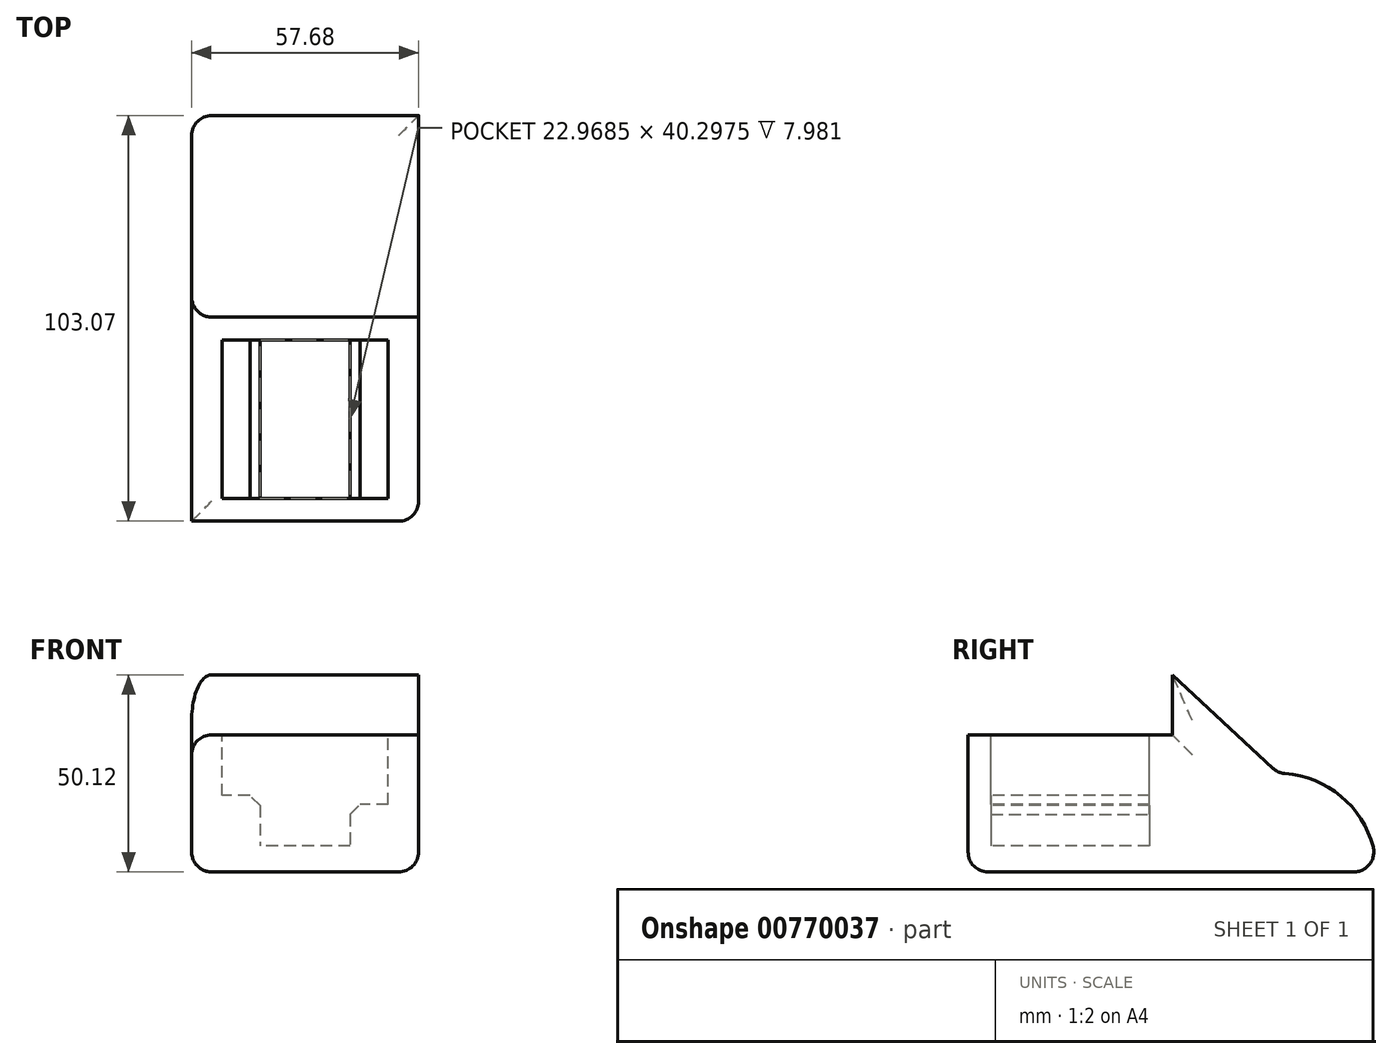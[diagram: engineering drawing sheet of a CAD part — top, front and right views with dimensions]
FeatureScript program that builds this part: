
annotation { "Feature Type Name" : "Feature", "Feature Type Description" : "" }
export const myFeature = defineFeature(function(context is Context, id is Id, definition is map)
    precondition{}
    {
        {
            var Q0;
            Q0=qCreatedBy(makeId("Top.planeOp"),FACE);
            var sketch = newSketch(context, id + "F0", { "sketchPlane" : qUnion([Q0])});
            skLineSegment(sketch, "E0.bottom", {"start": v(28.84, 51.86) * mm, "end": v(-28.84, 51.86) * mm});
            skLineSegment(sketch, "E0.top", {"start": v(28.84, -51.86) * mm, "end": v(-28.84, -51.86) * mm});
            skLineSegment(sketch, "E0.left", {"start": v(28.84, 51.86) * mm, "end": v(28.84, -51.86) * mm});
            skLineSegment(sketch, "E0.right", {"start": v(-28.84, 51.86) * mm, "end": v(-28.84, -51.86) * mm});
            skPoint(sketch, "E0.middle", {"position": v(0, 0) * mm});
            skSolve(sketch);
        }
        {
            var Q0;
            Q0 = qSketchRegion(id + "F0", true);
            extrude(context, id + "F1", {"entities" : qUnion([Q0]), "depth" : 50.12 * mm, "offsetDistance" : 25.4 * mm});
        }
        {
            var Q0;
            Q0=makeQuery(id+"F1.opExtrude","SWEPT_FACE",FACE,{"disambiguationData":[OSD([sQuery(id+"F0.wireOp",EDGE,"E0.left")])]});
            var sketch = newSketch(context, id + "F2", { "sketchPlane" : qUnion([Q0])});
            skArc(sketch, "E1", {"start": v(51.86, 0) * mm, "mid": v(44.58, 17.66) * mm, "end": v(26.97, 25.06) * mm});
            skPoint(sketch, "E1.endSnap0", {"position": v(51.86, 25.06) * mm});
            skLineSegment(sketch, "E2", {"start": v(26.97, 25.06) * mm, "end": v(0, 50.12) * mm});
            skLineSegment(sketch, "E3", {"start": v(0, 50.12) * mm, "end": v(0, 34.85) * mm});
            skLineSegment(sketch, "E4", {"start": v(0, 34.85) * mm, "end": v(-51.86, 34.85) * mm});
            skSolve(sketch);
        }
        {
            var Q0;
            Q0=makeQuery(id+"F2.imprint","IMPRINT",FACE,{"disambiguationData":[TD([[makeQuery(id+"F2.imprint","IMPRINT",EDGE,{"derivedFrom":sQuery(id+"F2.wireOp",EDGE,"E1")}),-1.0]])]});
            var Q1;
            {var subQ0=sQuery(id+"F2.wireOp",EDGE,"E3");Q1=makeQuery(id+"F2.imprint","IMPRINT",FACE,{"disambiguationData":[TD([[makeQuery(id+"F2.imprint","IMPRINT",EDGE,{"derivedFrom":subQ0}),-1.0]])]});}
            extrude(context, id + "F3", {"entities" : qUnion([Q0, Q1]), "operationType" : NewBodyOperationType.REMOVE, "oppositeDirection" : true, "depth" : 280.97 * mm, "offsetDistance" : 25.4 * mm});
        }
        {
            var Q0;
            Q0=makeQuery(id+"F3.boolean.opBoolean","COPY",FACE,{"derivedFrom":makeQuery(id+"F3.opExtrude","SWEPT_FACE",FACE,{"disambiguationData":[OSD([sQuery(id+"F2.wireOp",EDGE,"E4")])]})});
            var sketch = newSketch(context, id + "F4", { "sketchPlane" : qUnion([Q0])});
            skLineSegment(sketch, "E5.bottom", {"start": v(21.13, -5.78) * mm, "end": v(-21.13, -5.78) * mm});
            skLineSegment(sketch, "E5.top", {"start": v(21.13, -46.08) * mm, "end": v(-21.13, -46.08) * mm});
            skLineSegment(sketch, "E5.left", {"start": v(21.13, -5.78) * mm, "end": v(21.13, -46.08) * mm});
            skLineSegment(sketch, "E5.right", {"start": v(-21.13, -5.78) * mm, "end": v(-21.13, -46.08) * mm});
            skPoint(sketch, "E5.middle", {"position": v(0, -25.93) * mm});
            skPoint(sketch, "E5.middle.positionSnap0", {"position": v(-28.84, -25.93) * mm});
            skPoint(sketch, "E5.centerSnap0", {"position": v(-28.84, -25.93) * mm});
            skSolve(sketch);
        }
        {
            var Q0;
            Q0=makeQuery(id+"F4.imprint","IMPRINT",FACE,{"disambiguationData":[TD([[makeQuery(id+"F4.imprint","IMPRINT",EDGE,{"derivedFrom":sQuery(id+"F4.wireOp",EDGE,"E5.bottom")}),1.0]])]});
            extrude(context, id + "F5", {"entities" : qUnion([Q0]), "operationType" : NewBodyOperationType.REMOVE, "oppositeDirection" : true, "depth" : 28.22 * mm, "offsetDistance" : 25.4 * mm});
        }
        {
            var Q0;
            Q0=makeQuery(id+"F5.boolean.opBoolean","COPY",FACE,{"derivedFrom":makeQuery(id+"F5.opExtrude","CAP_FACE",FACE,{"disambiguationData":[OSD([sQuery(id+"F4.wireOp",EDGE,"E5.bottom"),sQuery(id+"F4.wireOp",EDGE,"E5.top"),sQuery(id+"F4.wireOp",EDGE,"E5.left"),sQuery(id+"F4.wireOp",EDGE,"E5.right")])],"isStart":false})});
            var sketch = newSketch(context, id + "F6", { "sketchPlane" : qUnion([Q0])});
            skLineSegment(sketch, "E6", {"start": v(-11.5, -5.78) * mm, "end": v(-11.5, -46.08) * mm});
            skSolve(sketch);
        }
        {
            var Q0;
            {var subQ0=sQuery(id+"F6.wireOp",EDGE,"E6");Q0=makeQuery(id+"F6.imprint","IMPRINT",FACE,{"disambiguationData":[TD([[makeQuery(id+"F6.imprint","IMPRINT",EDGE,{"derivedFrom":subQ0}),-1.0]])]});}
            var Q1;
            Q1 = qSketchRegion(id + "F6", true);
            extrude(context, id + "F7", {"entities" : qUnion([Q0, Q1]), "operationType" : NewBodyOperationType.ADD, "depth" : 12.77 * mm, "offsetDistance" : 25.4 * mm});
        }
        {
            var Q0;
            Q0=makeQuery(id+"F5.boolean.opBoolean","COPY",FACE,{"derivedFrom":makeQuery(id+"F5.opExtrude","CAP_FACE",FACE,{"disambiguationData":[OSD([sQuery(id+"F4.wireOp",EDGE,"E5.bottom"),sQuery(id+"F4.wireOp",EDGE,"E5.top"),sQuery(id+"F4.wireOp",EDGE,"E5.left"),sQuery(id+"F4.wireOp",EDGE,"E5.right")])],"isStart":false})});
            var sketch = newSketch(context, id + "F8", { "sketchPlane" : qUnion([Q0])});
            skLineSegment(sketch, "E7", {"start": v(11.47, -5.78) * mm, "end": v(11.47, -46.08) * mm});
            skSolve(sketch);
        }
        {
            var Q0;
            {var subQ0=sQuery(id+"F8.wireOp",EDGE,"E7");Q0=makeQuery(id+"F8.imprint","IMPRINT",FACE,{"disambiguationData":[TD([[makeQuery(id+"F8.imprint","IMPRINT",EDGE,{"derivedFrom":subQ0}),1.0]])]});}
            extrude(context, id + "F9", {"entities" : qUnion([Q0]), "operationType" : NewBodyOperationType.ADD, "depth" : 10.52 * mm, "offsetDistance" : 25.4 * mm});
        }
        {
            var Q0;
            Q0=makeQuery(id+"F3.boolean.opBoolean","COPY",EDGE,{"derivedFrom":makeQuery(id+"F3.opExtrude","CAP_EDGE",EDGE,{"disambiguationData":[OSD([sQuery(id+"F2.wireOp",EDGE,"E1")])],"isStart":true})});
            var Q1;
            Q1=makeQuery(id+"F3.boolean.opBoolean","COPY",EDGE,{"derivedFrom":makeQuery(id+"F3.opExtrude","CAP_EDGE",EDGE,{"disambiguationData":[OSD([sQuery(id+"F2.wireOp",EDGE,"E2")])],"isStart":true})});
            var Q2;
            Q2=makeQuery(id+"F3.boolean.opBoolean","COPY",EDGE,{"derivedFrom":makeQuery(id+"F3.opExtrude","SWEPT_EDGE",EDGE,{"disambiguationData":[OSD([sQuery(id+"F2.wireOp",EDGE,"E1"),sQuery(id+"F2.wireOp",EDGE,"E2")])]})});
            var Q3;
            Q3=makeQuery(id+"F3.boolean.opBoolean","INTERSECT",EDGE,{"derivedFrom":[makeQuery(id+"F1.opExtrude","SWEPT_FACE",FACE,{"disambiguationData":[OSD([sQuery(id+"F0.wireOp",EDGE,"E0.right")])]}),makeQuery(id+"F3.opExtrude","SWEPT_FACE",FACE,{"disambiguationData":[OSD([sQuery(id+"F2.wireOp",EDGE,"E2")])]})]});
            var Q4;
            Q4=makeQuery(id+"F3.boolean.opBoolean","INTERSECT",EDGE,{"derivedFrom":[makeQuery(id+"F1.opExtrude","SWEPT_FACE",FACE,{"disambiguationData":[OSD([sQuery(id+"F0.wireOp",EDGE,"E0.right")])]}),makeQuery(id+"F3.opExtrude","SWEPT_FACE",FACE,{"disambiguationData":[OSD([sQuery(id+"F2.wireOp",EDGE,"E1")])]})]});
            var Q5;
            {var subQ0=sQuery(id+"F0.wireOp",EDGE,"E0.bottom");Q5=makeQuery(id+"F3.boolean.opBoolean","MERGE",EDGE,{"derivedFrom":[makeQuery(id+"F1.opExtrude","CAP_EDGE",EDGE,{"disambiguationData":[OSD([subQ0])],"isStart":true}),makeQuery(id+"F3.opExtrude","SWEPT_EDGE",EDGE,{"disambiguationData":[OSD([subQ0,sQuery(id+"F0.wireOp",EDGE,"E0.left"),sQuery(id+"F2.wireOp",EDGE,"E1")])]})]});}
            var Q6;
            Q6=makeQuery(id+"F1.opExtrude","CAP_EDGE",EDGE,{"disambiguationData":[OSD([sQuery(id+"F0.wireOp",EDGE,"E0.left")])],"isStart":true});
            var Q7;
            Q7=makeQuery(id+"F3.boolean.opBoolean","COPY",EDGE,{"derivedFrom":makeQuery(id+"F3.opExtrude","CAP_EDGE",EDGE,{"disambiguationData":[OSD([sQuery(id+"F2.wireOp",EDGE,"E4")])],"isStart":true})});
            var Q8;
            Q8=makeQuery(id+"F1.opExtrude","SWEPT_EDGE",EDGE,{"disambiguationData":[OSD([sQuery(id+"F0.wireOp",EDGE,"E0.top"),sQuery(id+"F0.wireOp",EDGE,"E0.left")])]});
            var Q9;
            Q9=makeQuery(id+"F3.boolean.opBoolean","INTERSECT",EDGE,{"derivedFrom":[makeQuery(id+"F1.opExtrude","SWEPT_FACE",FACE,{"disambiguationData":[OSD([sQuery(id+"F0.wireOp",EDGE,"E0.right")])]}),makeQuery(id+"F3.opExtrude","SWEPT_FACE",FACE,{"disambiguationData":[OSD([sQuery(id+"F2.wireOp",EDGE,"E4")])]})]});
            var Q10;
            Q10=makeQuery(id+"F3.boolean.opBoolean","COPY",EDGE,{"derivedFrom":makeQuery(id+"F3.opExtrude","SWEPT_EDGE",EDGE,{"disambiguationData":[OSD([sQuery(id+"F0.wireOp",EDGE,"E0.top"),sQuery(id+"F0.wireOp",EDGE,"E0.left"),sQuery(id+"F2.wireOp",EDGE,"E4")])]})});
            var Q11;
            Q11=makeQuery(id+"F1.opExtrude","CAP_EDGE",EDGE,{"disambiguationData":[OSD([sQuery(id+"F0.wireOp",EDGE,"E0.top")])],"isStart":true});
            var Q12;
            Q12=makeQuery(id+"F1.opExtrude","CAP_EDGE",EDGE,{"disambiguationData":[OSD([sQuery(id+"F0.wireOp",EDGE,"E0.right")])],"isStart":true});
            var Q13;
            Q13=makeQuery(id+"F3.boolean.opBoolean","INTERSECT",EDGE,{"derivedFrom":[makeQuery(id+"F1.opExtrude","SWEPT_FACE",FACE,{"disambiguationData":[OSD([sQuery(id+"F0.wireOp",EDGE,"E0.right")])]}),makeQuery(id+"F3.opExtrude","SWEPT_FACE",FACE,{"disambiguationData":[OSD([sQuery(id+"F2.wireOp",EDGE,"E3")])]})]});
            var Q14;
            {var subQ0=sQuery(id+"F2.wireOp",EDGE,"E3");var subQ1=sQuery(id+"F2.wireOp",EDGE,"E2");var subQ2=sQuery(id+"F0.wireOp",EDGE,"E0.left");Q14=makeQuery(id+"F3.boolean.opBoolean","TWEAK_EDGE",EDGE,{"derivedFrom":[makeQuery(id+"F3.opExtrude","SWEPT_EDGE",EDGE,{"disambiguationData":[OSD([subQ2,subQ1,subQ0]),OD(0.0)]}),makeQuery(id+"F3.opExtrude","SWEPT_EDGE",EDGE,{"disambiguationData":[OSD([subQ2,subQ1,subQ0]),OD(1.0)]})]});}
            fillet(context, id + "F10", {"entities" : qUnion([Q0, Q1, Q2, Q3, Q4, Q5, Q6, Q7, Q8, Q9, Q10, Q11, Q12, Q13, Q14]), "radius" : 5.08 * mm, "tangentPropagation" : true, "allowEdgeOverflow" : false});
        }
        {
            var Q0;
            Q0=makeQuery(id+"F7.opExtrude","CAP_EDGE",EDGE,{"disambiguationData":[OSD([sQuery(id+"F6.wireOp",EDGE,"E6")])],"isStart":false});
            var Q1;
            Q1=makeQuery(id+"F9.opExtrude","CAP_EDGE",EDGE,{"disambiguationData":[OSD([sQuery(id+"F8.wireOp",EDGE,"E7")])],"isStart":false});
            chamfer(context, id + "F11", {"entities" : qUnion([Q0, Q1]), "width" : 2.54 * mm, "tangentPropagation" : true});
        }
    });
